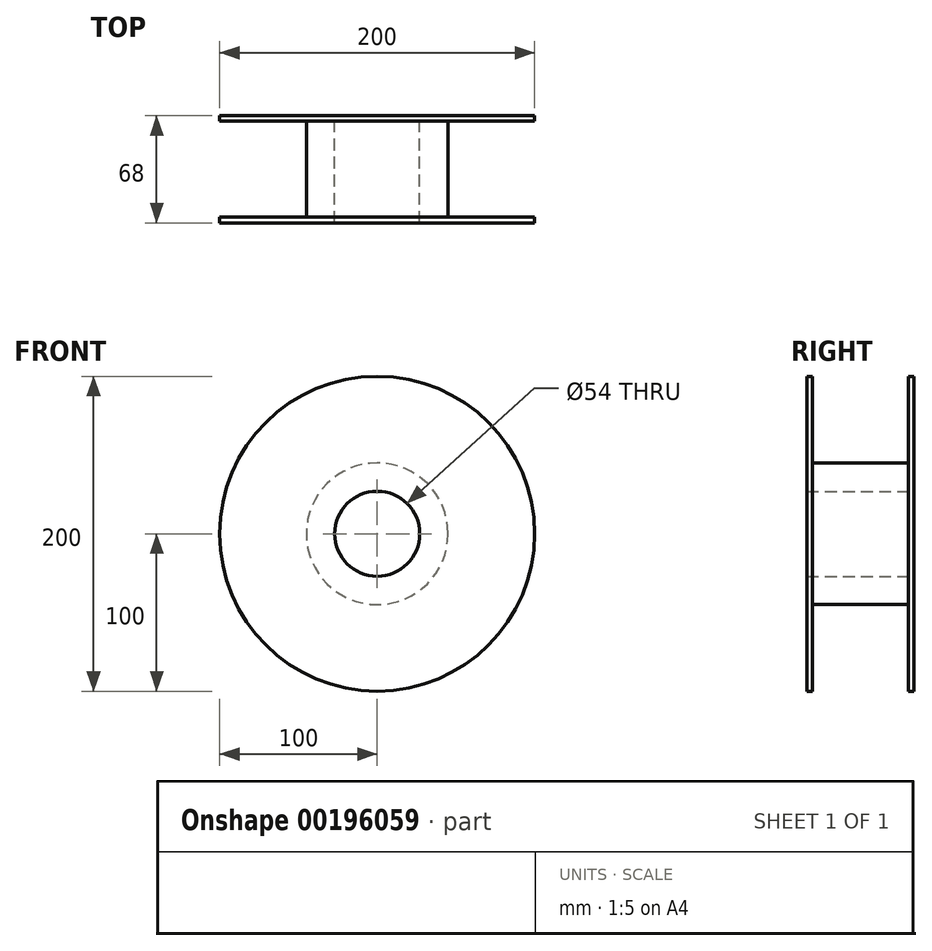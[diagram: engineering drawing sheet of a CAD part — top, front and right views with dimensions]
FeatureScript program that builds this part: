
annotation { "Feature Type Name" : "Feature", "Feature Type Description" : "" }
export const myFeature = defineFeature(function(context is Context, id is Id, definition is map)
    precondition{}
    {
        {
            var Q0;
            Q0=qCreatedBy(makeId("Front.planeOp"),FACE);
            var sketch = newSketch(context, id + "F0", { "sketchPlane" : qUnion([Q0])});
            skCircle(sketch, "E0", {"center": v(0, 0) * mm, "radius": 100 * mm});
            skCircle(sketch, "E1", {"center": v(0, 0) * mm, "radius": 27 * mm});
            skSolve(sketch);
        }
        {
            var Q0;
            Q0 = qSketchRegion(id + "F0", true);
            extrude(context, id + "F1", {"entities" : qUnion([Q0]), "depth" : 3.5 * mm});
        }
        {
            var Q0;
            Q0=makeQuery(id+"F1.opExtrude","CAP_FACE",FACE,{"disambiguationData":[OSD([sQuery(id+"F0.wireOp",EDGE,"E0"),sQuery(id+"F0.wireOp",EDGE,"E1")])],"isStart":true});
            var sketch = newSketch(context, id + "F2", { "sketchPlane" : qUnion([Q0])});
            skCircle(sketch, "E2", {"center": v(0, 0) * mm, "radius": 45 * mm});
            skCircle(sketch, "E3", {"center": v(0, 0) * mm, "radius": 27 * mm});
            skSolve(sketch);
        }
        {
            var Q0;
            Q0 = qSketchRegion(id + "F2", true);
            extrude(context, id + "F3", {"entities" : qUnion([Q0]), "operationType" : NewBodyOperationType.ADD, "depth" : 61 * mm});
        }
        {
            var Q0;
            Q0=makeQuery(id+"F3.opExtrude","CAP_FACE",FACE,{"disambiguationData":[OSD([sQuery(id+"F2.wireOp",EDGE,"E2"),sQuery(id+"F2.wireOp",EDGE,"E3")])],"isStart":false});
            var sketch = newSketch(context, id + "F4", { "sketchPlane" : qUnion([Q0])});
            skCircle(sketch, "E4", {"center": v(0, 0) * mm, "radius": 27 * mm});
            skCircle(sketch, "E5", {"center": v(0, 0) * mm, "radius": 100 * mm});
            skSolve(sketch);
        }
        {
            var Q0;
            Q0 = qSketchRegion(id + "F4", true);
            extrude(context, id + "F5", {"entities" : qUnion([Q0]), "operationType" : NewBodyOperationType.ADD, "depth" : 3.5 * mm});
        }
    });
